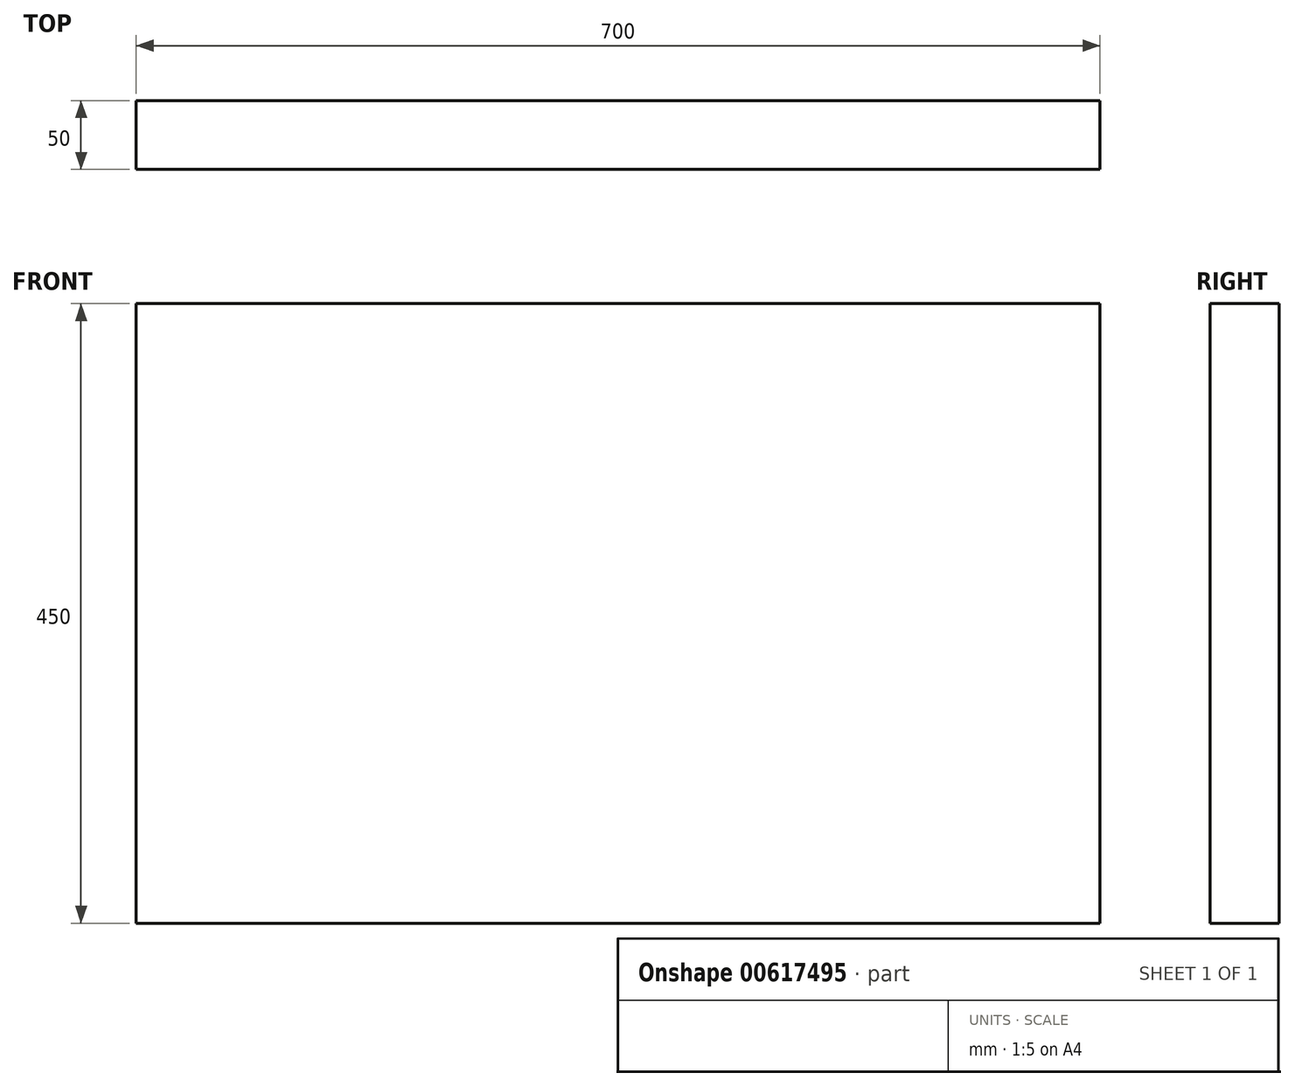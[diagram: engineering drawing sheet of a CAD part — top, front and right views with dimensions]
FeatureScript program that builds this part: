
annotation { "Feature Type Name" : "Feature", "Feature Type Description" : "" }
export const myFeature = defineFeature(function(context is Context, id is Id, definition is map)
    precondition{}
    {
        {
            var Q0;
            Q0=qCreatedBy(makeId("Top.planeOp"),FACE);
            var sketch = newSketch(context, id + "F0", { "sketchPlane" : qUnion([Q0])});
            skLineSegment(sketch, "E0.bottom", {"start": v(-376.76, 35.55) * mm, "end": v(323.24, 35.55) * mm});
            skLineSegment(sketch, "E0.top", {"start": v(-376.76, -14.45) * mm, "end": v(323.24, -14.45) * mm});
            skLineSegment(sketch, "E0.left", {"start": v(-376.76, 35.55) * mm, "end": v(-376.76, -14.45) * mm});
            skLineSegment(sketch, "E0.right", {"start": v(323.24, 35.55) * mm, "end": v(323.24, -14.45) * mm});
            skSolve(sketch);
        }
        {
            var Q0;
            Q0=makeQuery(id+"F0.imprint","IMPRINT",FACE,{"disambiguationData":[TD([[makeQuery(id+"F0.imprint","IMPRINT",EDGE,{"derivedFrom":sQuery(id+"F0.wireOp",EDGE,"E0.bottom")}),-1.0]])]});
            extrude(context, id + "F1", {"entities" : qUnion([Q0]), "depth" : 450 * mm, "offsetDistance" : 25 * mm});
        }
    });
